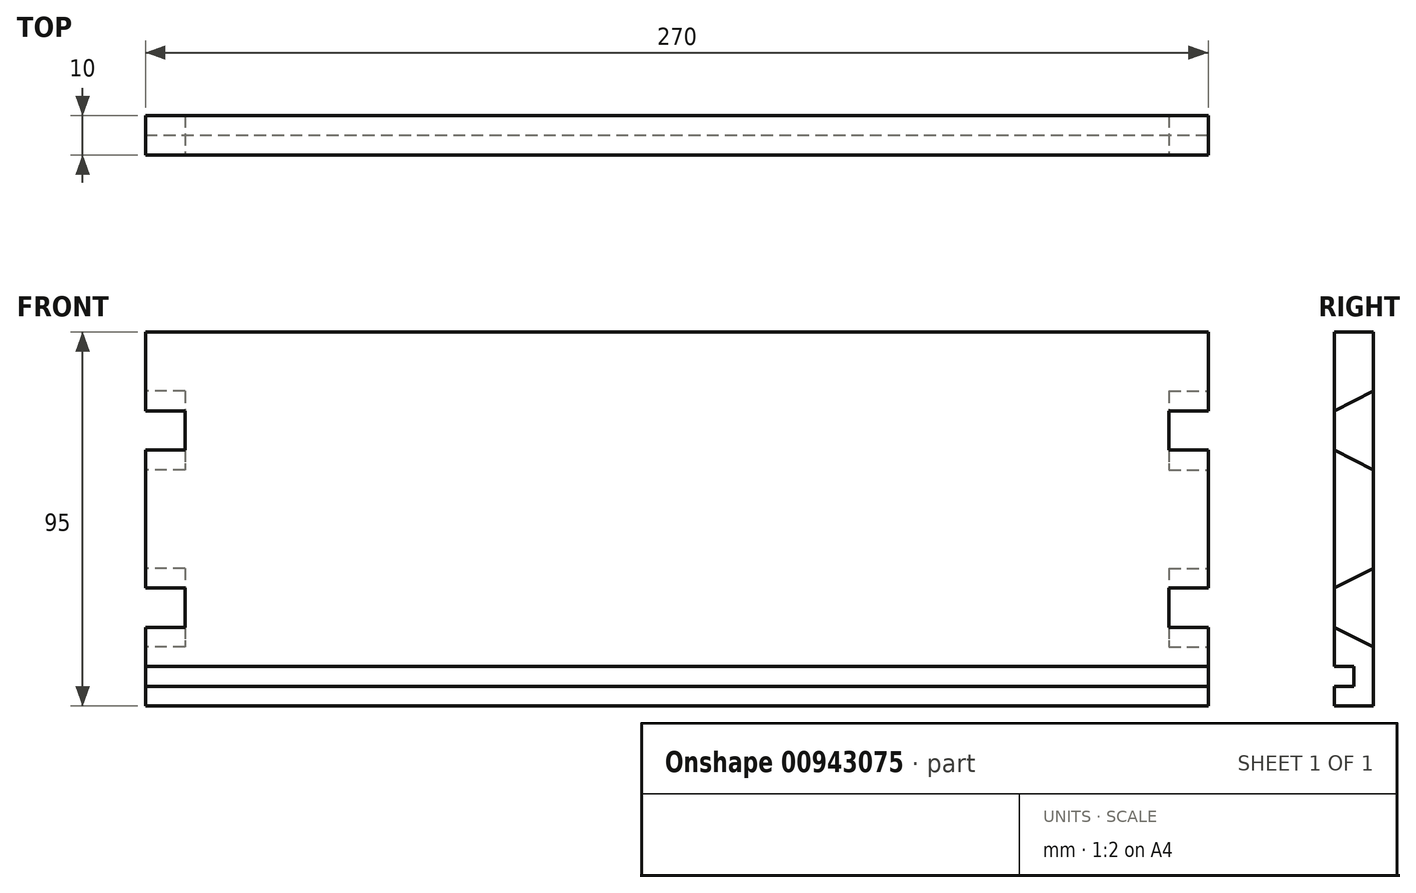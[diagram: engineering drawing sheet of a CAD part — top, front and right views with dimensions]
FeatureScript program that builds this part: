
annotation { "Feature Type Name" : "Feature", "Feature Type Description" : "" }
export const myFeature = defineFeature(function(context is Context, id is Id, definition is map)
    precondition{}
    {
        {
            var Q0;
            Q0=qCreatedBy(makeId("Front.planeOp"),FACE);
            var sketch = newSketch(context, id + "F0", { "sketchPlane" : qUnion([Q0])});
            skLineSegment(sketch, "E0.bottom", {"start": v(67.05, 54.96) * mm, "end": v(-67.95, 54.96) * mm});
            skLineSegment(sketch, "E0.top", {"start": v(67.05, -40.04) * mm, "end": v(-67.95, -40.04) * mm});
            skLineSegment(sketch, "E0.left", {"start": v(67.05, 54.96) * mm, "end": v(67.05, -40.04) * mm});
            skLineSegment(sketch, "E0.right", {"start": v(-67.95, 54.96) * mm, "end": v(-67.95, -40.04) * mm});
            skSolve(sketch);
        }
        {
            var Q0;
            Q0 = qSketchRegion(id + "F0", true);
            extrude(context, id + "F1", {"entities" : qUnion([Q0]), "depth" : 10 * mm, "offsetDistance" : 25 * mm});
        }
        {
            var Q0;
            Q0=makeQuery(id+"F1.opExtrude","SWEPT_FACE",FACE,{"disambiguationData":[OSD([sQuery(id+"F0.wireOp",EDGE,"E0.right")])]});
            var sketch = newSketch(context, id + "F2", { "sketchPlane" : qUnion([Q0])});
            skLineSegment(sketch, "E1", {"start": v(0, 39.96) * mm, "end": v(10, 34.96) * mm});
            skLineSegment(sketch, "E2", {"start": v(10, 34.96) * mm, "end": v(10, 24.96) * mm});
            skLineSegment(sketch, "E3", {"start": v(10, 24.96) * mm, "end": v(0, 19.96) * mm});
            skLineSegment(sketch, "E4", {"start": v(0, 19.96) * mm, "end": v(0, -5.04) * mm});
            skLineSegment(sketch, "E5", {"start": v(0, -5.04) * mm, "end": v(10, -10.04) * mm});
            skLineSegment(sketch, "E6", {"start": v(10, -10.04) * mm, "end": v(10, -20.04) * mm});
            skLineSegment(sketch, "E7", {"start": v(10, -20.04) * mm, "end": v(0, -25.04) * mm});
            skSolve(sketch);
        }
        {
            var Q0;
            {var subQ0=sQuery(id+"F2.wireOp",EDGE,"E1");Q0=makeQuery(id+"F2.imprint","IMPRINT",FACE,{"disambiguationData":[TD([[makeQuery(id+"F2.imprint","IMPRINT",EDGE,{"derivedFrom":subQ0}),-1.0]])]});}
            var Q1;
            {var subQ0=sQuery(id+"F2.wireOp",EDGE,"E5");Q1=makeQuery(id+"F2.imprint","IMPRINT",FACE,{"disambiguationData":[TD([[makeQuery(id+"F2.imprint","IMPRINT",EDGE,{"derivedFrom":subQ0}),-1.0]])]});}
            extrude(context, id + "F3", {"entities" : qUnion([Q0, Q1]), "operationType" : NewBodyOperationType.REMOVE, "oppositeDirection" : true, "depth" : 10 * mm, "offsetDistance" : 25 * mm});
        }
        {
            var Q0;
            Q0=makeQuery(id+"F1.opExtrude","CAP_FACE",FACE,{"disambiguationData":[OSD([sQuery(id+"F0.wireOp",EDGE,"E0.bottom"),sQuery(id+"F0.wireOp",EDGE,"E0.top"),sQuery(id+"F0.wireOp",EDGE,"E0.left"),sQuery(id+"F0.wireOp",EDGE,"E0.right")])],"isStart":false});
            var sketch = newSketch(context, id + "F4", { "sketchPlane" : qUnion([Q0])});
            skLineSegment(sketch, "E8.bottom", {"start": v(-67.95, -30.04) * mm, "end": v(67.05, -30.04) * mm});
            skLineSegment(sketch, "E8.top", {"start": v(-67.95, -35.04) * mm, "end": v(67.05, -35.04) * mm});
            skLineSegment(sketch, "E8.left", {"start": v(-67.95, -30.04) * mm, "end": v(-67.95, -35.04) * mm});
            skLineSegment(sketch, "E8.right", {"start": v(67.05, -30.04) * mm, "end": v(67.05, -35.04) * mm});
            skSolve(sketch);
        }
        {
            var Q0;
            Q0=makeQuery(id+"F4.imprint","IMPRINT",FACE,{"disambiguationData":[TD([[makeQuery(id+"F4.imprint","IMPRINT",EDGE,{"derivedFrom":sQuery(id+"F4.wireOp",EDGE,"E8.bottom")}),-1.0]])]});
            extrude(context, id + "F5", {"entities" : qUnion([Q0]), "operationType" : NewBodyOperationType.REMOVE, "oppositeDirection" : true, "depth" : 5 * mm, "offsetDistance" : 25 * mm});
        }
        {
            var Q0;
            Q0=makeQuery(id+"F1.opExtrude","SWEPT_BODY",BODY,{"disambiguationData":[OSD([sQuery(id+"F0.wireOp",EDGE,"E0.bottom"),sQuery(id+"F0.wireOp",EDGE,"E0.top"),sQuery(id+"F0.wireOp",EDGE,"E0.left"),sQuery(id+"F0.wireOp",EDGE,"E0.right")])]});
            var Q1;
            Q1=makeQuery(id+"F1.opExtrude","SWEPT_FACE",FACE,{"disambiguationData":[OSD([sQuery(id+"F0.wireOp",EDGE,"E0.left")])]});
            mirror(context, id + "F6", {"operationType" : NewBodyOperationType.ADD, "entities" : qUnion([Q0]), "mirrorPlane" : qUnion([Q1])});
        }
    });
